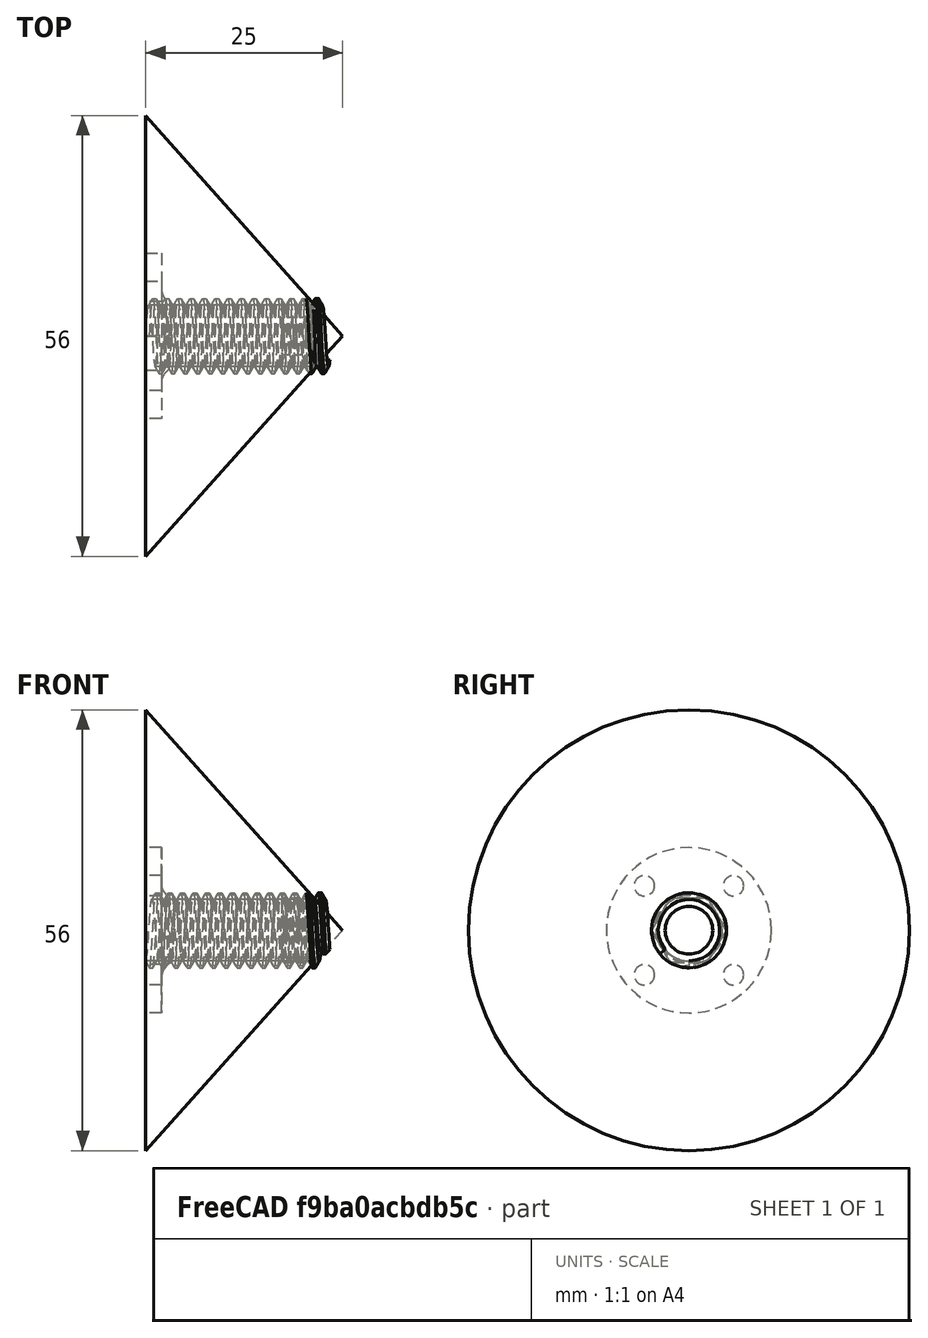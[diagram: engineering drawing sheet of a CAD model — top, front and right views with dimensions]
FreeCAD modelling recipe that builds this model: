
FCSTD DOCUMENT  (FreeCAD 0.20R27422 (Git))
Label: anchor
License: All rights reserved
LicenseURL: http://en.wikipedia.org/wiki/All_rights_reserved
objects: Sketcher::SketchObject×5, TechDraw::DrawProjGroupItem×4, PartDesign::Body×3, PartDesign::Pad×2, PartDesign::Boolean×2, PartDesign::Plane×2, PartDesign::Pocket×2, Spreadsheet::Sheet×1, PartDesign::AdditiveHelix×1, PartDesign::Fillet×1, PartDesign::AdditiveCone×1, TechDraw::DrawSVGTemplate×1, TechDraw::DrawProjGroup×1, TechDraw::DrawPage×1
note: 26 computed .brp shape members not serialized (recipe doc carries the construction recipe); baked Part::Feature solids carry a one-line shape summary decoded from their .brp

FEATURE [Sketcher::SketchObject] Sketch
  FullyConstrained = true
  MapMode = 5
  Placement = pos=(0,0,0) rot=(1,0,0;1.5708rad)
  Support = -> [XZ_Plane]
  expr: .Constraints.P = Spreadsheet.pitch
  expr: Constraints[24] = Spreadsheet.diameter / 2
  expr: Constraints[3] = Spreadsheet.pitch / 4
  expr: Constraints[4] = Spreadsheet.pitch / 8
  sketch-geometry (9):
    g0: LineSegment StartX=0 StartY=-3.90574 StartZ=0 EndX=0.496094 EndY=-4.765 EndZ=0
    g1: LineSegment StartX=0.496094 StartY=-4.765 StartZ=0 EndX=0.892969 EndY=-4.765 EndZ=0
    g2: LineSegment StartX=0.892969 StartY=-4.765 StartZ=0 EndX=1.38906 EndY=-3.90574 EndZ=0
    g3: LineSegment StartX=1.38906 StartY=-3.90574 StartZ=0 EndX=1.5875 EndY=-3.90574 EndZ=0
    g4: LineSegment StartX=0 StartY=-3.90574 StartZ=0 EndX=1.38906 EndY=-3.90574 EndZ=0
    g5: LineSegment StartX=0.496094 StartY=-4.765 StartZ=0 EndX=0.694531 EndY=-5.1087 EndZ=0
    g6: LineSegment StartX=0.892969 StartY=-4.765 StartZ=0 EndX=0.694531 EndY=-5.1087 EndZ=0
    g7: LineSegment StartX=1.38906 StartY=-3.90574 StartZ=0 EndX=1.48828 EndY=-3.73389 EndZ=0
    g8: LineSegment StartX=1.48828 StartY=-3.73389 StartZ=0 EndX=1.5875 EndY=-3.90574 EndZ=0
  constraints (26):
    c: Angle(g2,g0) = 1.0472
    c: Angle(g0,g-2) = 2.61799
    c: DistanceX(g0,g3) = 1.5875  'P'
    c: DistanceX(g1,g1) = 0.396875
    c: DistanceX(g3,g3) = 0.198437
    c: Coincident(g4,g2)
    c: Coincident(g4,g0)
    c: Coincident(g0,g1)
    c: Coincident(g2,g1)
    c: Coincident(g3,g2)
    c: Parallel(g3,g4)
    c: Parallel(g4,g-1)
    c: Parallel(g-1,g1)
    c: PointOnObject(g0,g-2)
    c: Coincident(g5,g0)
    c: Coincident(g6,g1)
    c: Coincident(g6,g5)
    c: Parallel(g5,g0)
    c: Parallel(g6,g2)
    c: Coincident(g7,g2)
    c: Coincident(g8,g7)
    c: Parallel(g7,g2)
    c: Parallel(g5,g8)
    c: Coincident(g8,g3)
    c: DistanceY(g0,g-1) = 4.765
    c: DistanceY(g0,g-1) = 3.90574
FEATURE [Spreadsheet::Sheet] Spreadsheet
  cells = A1=threads per inch; B1=16; A2=threads per mm; B2==B1 / 25.4; A3=pitch (mm); B3(pitch)==1 / B2; A4=diameter (mm); B4(diameter)=9.529999999999999
FEATURE [PartDesign::AdditiveHelix] AdditiveHelix
  Angle = 0
  Axis = (1,0,0)
  Base = (0,0,0)
  Growth = 0
  HasBeenEdited = true
  Height = 22
  LeftHanded = false
  Mode = 0
  Outside = false
  Pitch = 1.5875
  Placement = pos=(0,0,0) rot=(1,0,0;1.5708rad)
  Profile = -> Sketch
  ReferenceAxis = -> Sketch [H_Axis]
  Turns = 13.8583
  expr: Pitch = Spreadsheet.pitch
FEATURE [PartDesign::Body] Body  label="thread"
  Group = -> [Sketch,AdditiveHelix]
  Origin = -> Origin
  Tip = -> AdditiveHelix
FEATURE [Sketcher::SketchObject] Sketch001
  FullyConstrained = true
  MapMode = 5
  Placement = pos=(0,0,0) rot=(0.57735,0.57735,0.57735;2.0944rad)
  Support = -> [YZ_Plane001]
  sketch-geometry (11):
    g0: Circle CenterX=0 CenterY=0 CenterZ=0 NormalX=0 NormalY=0 NormalZ=1 AngleXU=0 Radius=10.5
    g1: LineSegment StartX=5.65685 StartY=-5.65685 StartZ=0 EndX=5.65685 EndY=5.65685 EndZ=0
    g2: LineSegment StartX=5.65685 StartY=5.65685 StartZ=0 EndX=-5.65685 EndY=5.65685 EndZ=0
    g3: LineSegment StartX=-5.65685 StartY=5.65685 StartZ=0 EndX=-5.65685 EndY=-5.65685 EndZ=0
    g4: LineSegment StartX=-5.65685 StartY=-5.65685 StartZ=0 EndX=5.65685 EndY=-5.65685 EndZ=0
    g5: Circle CenterX=0 CenterY=0 CenterZ=0 NormalX=0 NormalY=0 NormalZ=1 AngleXU=0 Radius=8
    g6: Circle CenterX=-5.65685 CenterY=5.65685 CenterZ=0 NormalX=0 NormalY=0 NormalZ=1 AngleXU=0 Radius=1.3
    g7: Circle CenterX=5.65685 CenterY=5.65685 CenterZ=0 NormalX=0 NormalY=0 NormalZ=1 AngleXU=0 Radius=1.3
    g8: Circle CenterX=5.65685 CenterY=-5.65685 CenterZ=0 NormalX=0 NormalY=0 NormalZ=1 AngleXU=0 Radius=1.3
    g9: Circle CenterX=-5.65685 CenterY=-5.65685 CenterZ=0 NormalX=0 NormalY=0 NormalZ=1 AngleXU=0 Radius=1.3
    g10: Circle CenterX=-5.65685 CenterY=5.65685 CenterZ=0 NormalX=0 NormalY=0 NormalZ=1 AngleXU=0 Radius=1.78562
  constraints (26):
    c: Coincident(g0,g-1)
    c: Diameter(g0) = 21
    c: Coincident(g1,g2)
    c: Coincident(g2,g3)
    c: Coincident(g3,g4)
    c: Coincident(g4,g1)
    c: Equal(g1,g2)
    c: Equal(g1,g3)
    c: Equal(g1,g4)
    c: PointOnObject(g1,g5)
    c: PointOnObject(g2,g5)
    c: PointOnObject(g3,g5)
    c: PointOnObject(g4,g5)
    c: Coincident(g5,g0)
    c: Parallel(g2,g-1)
    c: Coincident(g6,g2)
    c: Diameter(g6) = 2.6
    c: Diameter(g5) = 16
    c: Coincident(g7,g1)
    c: Coincident(g8,g1)
    c: Coincident(g9,g3)
    c: Equal(g9,g8)
    c: Equal(g8,g7)
    c: Equal(g7,g6)
    c: Coincident(g10,g6)
    c: Diameter(g10) = 3.57124
FEATURE [PartDesign::Pad] Pad
  Direction = (1,1,1)
  Length = 2
  Length2 = 100
  Placement = pos=(0,0,0) rot=(0.57735,0.57735,0.57735;2.0944rad)
  Profile = -> Sketch001
  Type = 0
FEATURE [Sketcher::SketchObject] Sketch003
  FullyConstrained = true
  MapMode = 5
  Placement = pos=(0,0,0) rot=(0.57735,0.57735,0.57735;2.0944rad)
  Support = -> [YZ_Plane001]
  expr: Constraints[1] = 3.91 * 2
  sketch-geometry (1):
    g0: Circle CenterX=0 CenterY=0 CenterZ=0 NormalX=0 NormalY=0 NormalZ=1 AngleXU=0 Radius=3.91
  constraints (2):
    c: Coincident(g0,g-1)
    c: Diameter(g0) = 7.82
FEATURE [PartDesign::Pad] Pad001
  BaseFeature = -> Pad
  Direction = (1,-2e-16,3e-16)
  Length = 25
  Length2 = 100
  Placement = pos=(0,0,0) rot=(0.57735,0.57735,0.57735;2.0944rad)
  Profile = -> Sketch003
  Type = 0
FEATURE [PartDesign::Fillet] Fillet
  Base = -> Pad001 [Edge12]
  BaseFeature = -> Pad001
  Placement = pos=(0,0,0) rot=(0.57735,0.57735,0.57735;2.0944rad)
  Radius = 2.1
  SupportTransform = false
  UseAllEdges = false
FEATURE [PartDesign::Boolean] Boolean
  BaseFeature = -> Fillet
  Group = -> [Body]
  Type = 0
FEATURE [PartDesign::AdditiveCone] Cone
  Angle = 360
  AttacherType = Attacher::AttachEngine3D
  Height = 25
  MapMode = 5
  Placement = pos=(0,0,0) rot=(0.57735,0.57735,0.57735;2.0944rad)
  Radius1 = 28
  Radius2 = 0
  Support = -> [YZ_Plane004]
FEATURE [PartDesign::Body] Body004  label="cone"
  Group = -> [Cone]
  Origin = -> Origin004
  Tip = -> Cone
FEATURE [PartDesign::Boolean] Boolean001
  BaseFeature = -> Boolean
  Group = -> [Body004]
  Type = 2
FEATURE [PartDesign::Plane] DatumPlane
  AttachmentOffset = pos=(0,0,17.3) rot=(0,0,1;0rad)
  Length = 60
  MapMode = 5
  Placement = pos=(17.3,-3.8e-15,3.8e-15) rot=(0.57735,0.57735,0.57735;2.0944rad)
  ResizeMode = 0
  Support = -> [YZ_Plane001]
  Width = 60
FEATURE [Sketcher::SketchObject] Sketch004
  FullyConstrained = true
  MapMode = 5
  Placement = pos=(17.3,-3.8e-15,3.8e-15) rot=(0.57735,0.57735,0.57735;2.0944rad)
  Support = -> [DatumPlane]
  sketch-geometry (9):
    g0: LineSegment StartX=2.36714 StartY=-4.1 StartZ=0 EndX=4.73427 EndY=0 EndZ=0
    g1: LineSegment StartX=4.73427 StartY=0 StartZ=0 EndX=2.36714 EndY=4.1 EndZ=0
    g2: LineSegment StartX=2.36714 StartY=4.1 StartZ=0 EndX=-2.36714 EndY=4.1 EndZ=0
    g3: LineSegment StartX=-2.36714 StartY=4.1 StartZ=0 EndX=-4.73427 EndY=2.4887e-12 EndZ=0
    g4: LineSegment StartX=-4.73427 StartY=2.4885e-12 StartZ=0 EndX=-2.36714 EndY=-4.1 EndZ=0
    g5: LineSegment StartX=-2.36714 StartY=-4.1 StartZ=0 EndX=2.36714 EndY=-4.1 EndZ=0
    g6: Circle CenterX=0 CenterY=0 CenterZ=0 NormalX=0 NormalY=0 NormalZ=1 AngleXU=0 Radius=4.73427
    g7: Circle CenterX=0 CenterY=0 CenterZ=0 NormalX=0 NormalY=0 NormalZ=1 AngleXU=0 Radius=15
    g8: Circle CenterX=0 CenterY=0 CenterZ=0 NormalX=0 NormalY=0 NormalZ=1 AngleXU=0 Radius=4.1
  constraints (20):
    c: Coincident(g0,g1)
    c: Coincident(g1,g2)
    c: Coincident(g2,g3)
    c: Coincident(g3,g4)
    c: Coincident(g4,g5)
    c: Coincident(g5,g0)
    c: Equal(g0, g1-g5) x5
    c: PointOnObject(g0,g6)
    c: PointOnObject(g1,g6)
    c: PointOnObject(g2,g6)
    c: PointOnObject(g3,g6)
    c: PointOnObject(g4,g6)
    c: PointOnObject(g5,g6)
    c: Coincident(g6,g-1)
    c: PointOnObject(g0,g-1)
    c: Coincident(g7,g-1)
    c: Diameter(g7) = 30
    c: Coincident(g8,g7)
    c: Tangent(g8,g2)
    c: Diameter(g8) = 8.2
FEATURE [PartDesign::Pocket] Pocket
  BaseFeature = -> Boolean001
  Direction = (-1,1e-16,-1e-16)
  Length = 5
  Length2 = 5
  Profile = -> Sketch004
  ReferenceAxis = -> Sketch004 [N_Axis]
  Reversed = true
  Type = 0
FEATURE [PartDesign::Plane] DatumPlane001
  AttachmentOffset = pos=(0,0,5) rot=(0,0,1;0rad)
  Length = 60
  MapMode = 5
  Placement = pos=(22.3,-4.4e-15,4.4e-15) rot=(0.57735,0.57735,0.57735;2.0944rad)
  ResizeMode = 0
  Support = -> [DatumPlane]
  Width = 60
FEATURE [Sketcher::SketchObject] Sketch005
  FullyConstrained = true
  MapMode = 5
  Placement = pos=(22.3,-4.4e-15,4.4e-15) rot=(0.57735,0.57735,0.57735;2.0944rad)
  Support = -> [DatumPlane001]
  sketch-geometry (1):
    g0: Circle CenterX=0 CenterY=0 CenterZ=0 NormalX=0 NormalY=0 NormalZ=1 AngleXU=0 Radius=16.225
  constraints (2):
    c: Coincident(g0,g-1)
    c: Diameter(g0) = 32.45
FEATURE [PartDesign::Pocket] Pocket001
  BaseFeature = -> Pocket
  Direction = (-1,0,0)
  Length = 5
  Length2 = 5
  Profile = -> Sketch005
  ReferenceAxis = -> Sketch005 [N_Axis]
  Reversed = true
  Type = 1
FEATURE [PartDesign::Body] Body001  label="base"
  Group = -> [Sketch001,Pad,Sketch003,Pad001,Fillet,Boolean,Boolean001,DatumPlane,Sketch004,Pocket,DatumPlane001,Sketch005,Pocket001]
  Origin = -> Origin001
  Tip = -> Pocket001
FEATURE [TechDraw::DrawSVGTemplate] Template
  EditableTexts = Designed_by_Name=Designed by Name; Drawing_number=Drawing number; FC-Date=Date; FC-SC=Scale; FC-SH=Sheet; FC-Title=Title; Subtitle=Subtitle; Weight=Weight
  Height = 210
  Orientation = 1
  Width = 297
FEATURE [TechDraw::DrawProjGroupItem] ProjItem  label="Front"
  CoarseView = false
  Direction = (1,0,0)
  Focus = 100
  HardHidden = false
  IsoCount = 0
  IsoHidden = false
  IsoVisible = false
  LockPosition = true
  Perspective = false
  Rotation = 0
  RotationVector = (0,-1,0)
  Scale = 3
  ScaleType = 2
  SeamHidden = false
  SeamVisible = true
  SmoothHidden = false
  SmoothVisible = true
  Source = -> [Body001]
  Type = 0
  X = 0
  XDirection = (0,-1,0)
  Y = 0
FEATURE [TechDraw::DrawProjGroupItem] ProjItem001  label="FrontTopRight"
  CoarseView = false
  Direction = (0.57735,-0.57735,-0.57735)
  Focus = 100
  HardHidden = false
  IsoCount = 0
  IsoHidden = false
  IsoVisible = false
  LockPosition = false
  Perspective = false
  Rotation = 0
  RotationVector = (1,0,0)
  Scale = 3
  ScaleType = 2
  SeamHidden = false
  SeamVisible = true
  SmoothHidden = false
  SmoothVisible = true
  Source = -> [Body001]
  Type = 7
  X = -92.279
  XDirection = (-0.707107,-0.707107,0)
  Y = -96.8733
FEATURE [TechDraw::DrawProjGroupItem] ProjItem002  label="Right"
  CoarseView = false
  Direction = (1e-16,-1,0)
  Focus = 100
  HardHidden = false
  IsoCount = 0
  IsoHidden = false
  IsoVisible = false
  LockPosition = false
  Perspective = false
  Rotation = 0
  RotationVector = (1,0,0)
  Scale = 3
  ScaleType = 2
  SeamHidden = false
  SeamVisible = true
  SmoothHidden = false
  SmoothVisible = true
  Source = -> [Body001]
  Type = 2
  X = -86.8797
  XDirection = (-1,-1e-16,0)
  Y = 0
FEATURE [TechDraw::DrawProjGroupItem] ProjItem003  label="Top"
  CoarseView = false
  Direction = (0,0,-1)
  Focus = 100
  HardHidden = false
  IsoCount = 0
  IsoHidden = false
  IsoVisible = false
  LockPosition = false
  Perspective = false
  Rotation = 0
  RotationVector = (1,0,0)
  Scale = 3
  ScaleType = 2
  SeamHidden = false
  SeamVisible = true
  SmoothHidden = false
  SmoothVisible = true
  Source = -> [Body001]
  Type = 4
  X = 0
  XDirection = (0,-1,0)
  Y = -96.2507
FEATURE [TechDraw::DrawProjGroup] ProjGroup
  Anchor = -> ProjItem
  AutoDistribute = true
  LockPosition = false
  ProjectionType = 0
  Rotation = 0
  Scale = 3
  ScaleType = 2
  Source = -> [Body001]
  Views = -> [ProjItem,ProjItem001,ProjItem002,ProjItem003]
  X = 148.5
  Y = 160
  spacingX = 15
  spacingY = 15
FEATURE [TechDraw::DrawPage] Page
  KeepUpdated = true
  NextBalloonIndex = 1
  ProjectionType = 0
  Template = -> Template
  Views = -> [ProjGroup]
